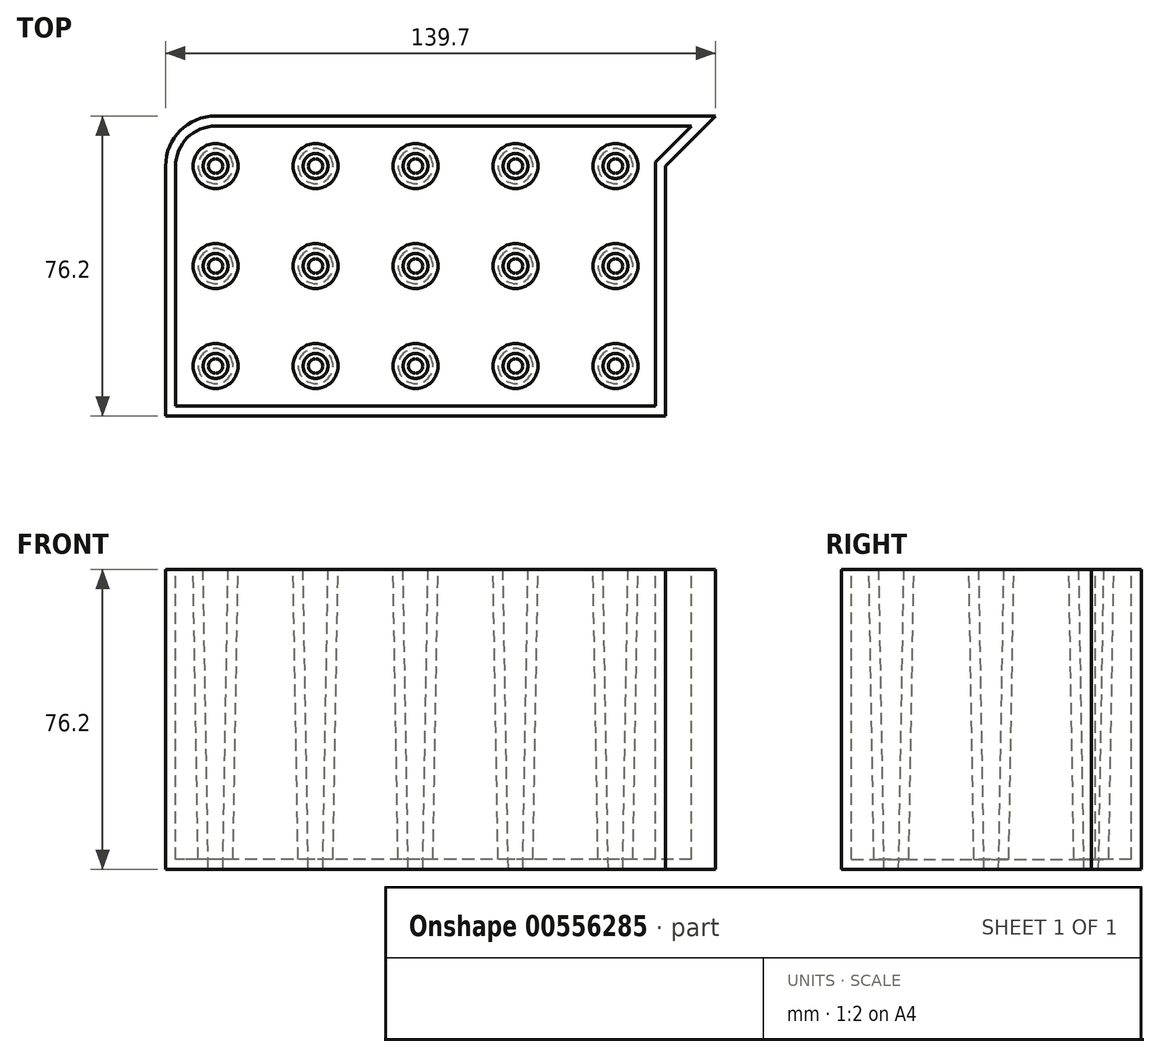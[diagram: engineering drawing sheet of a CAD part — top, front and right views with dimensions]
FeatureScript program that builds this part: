
annotation { "Feature Type Name" : "Feature", "Feature Type Description" : "" }
export const myFeature = defineFeature(function(context is Context, id is Id, definition is map)
    precondition{}
    {
        {
            var Q0;
            Q0=qCreatedBy(makeId("Top.planeOp"),FACE);
            var sketch = newSketch(context, id + "F0", { "sketchPlane" : qUnion([Q0])});
            skLineSegment(sketch, "E0.bottom", {"start": v(63.5, -38.1) * mm, "end": v(-63.5, -38.1) * mm});
            skLineSegment(sketch, "E0.top", {"start": v(76.2, 38.1) * mm, "end": v(-50.8, 38.1) * mm});
            skLineSegment(sketch, "E0.left", {"start": v(63.5, -38.1) * mm, "end": v(63.5, 25.4) * mm});
            skLineSegment(sketch, "E0.right", {"start": v(-63.5, -38.1) * mm, "end": v(-63.5, 25.4) * mm});
            skPoint(sketch, "E0.middle", {"position": v(0, 0) * mm});
            skPoint(sketch, "E1.visualSharp", {"position": v(-63.5, 38.1) * mm});
            skArc(sketch, "E1.filletArc", {"start": v(-50.8, 38.1) * mm, "mid": v(-59.78, 34.38) * mm, "end": v(-63.5, 25.4) * mm});
            skLineSegment(sketch, "E2", {"start": v(76.2, 38.1) * mm, "end": v(63.5, 25.4) * mm});
            skPoint(sketch, "E3.orphan", {"position": v(63.5, 38.1) * mm});
            skSolve(sketch);
        }
        {
            var Q0;
            Q0=makeQuery(id+"F0.imprint","IMPRINT",FACE,{"disambiguationData":[TD([[makeQuery(id+"F0.imprint","IMPRINT",EDGE,{"derivedFrom":sQuery(id+"F0.wireOp",EDGE,"E0.bottom")}),-1.0]])]});
            extrude(context, id + "F1", {"entities" : qUnion([Q0]), "oppositeDirection" : true, "depth" : 76.2 * mm, "offsetDistance" : 25.4 * mm});
        }
        {
            var Q0;
            Q0=makeQuery(id+"F1.opExtrude","CAP_FACE",FACE,{"disambiguationData":[OSD([sQuery(id+"F0.wireOp",EDGE,"E0.bottom"),sQuery(id+"F0.wireOp",EDGE,"E0.top"),sQuery(id+"F0.wireOp",EDGE,"E0.left"),sQuery(id+"F0.wireOp",EDGE,"E0.right"),sQuery(id+"F0.wireOp",EDGE,"E1.filletArc"),sQuery(id+"F0.wireOp",EDGE,"E2")])],"isStart":true});
            var sketch = newSketch(context, id + "F2", { "sketchPlane" : qUnion([Q0])});
            skCircle(sketch, "E4", {"center": v(-50.8, 25.4) * mm, "radius": 3.18 * mm});
            skCircle(sketch, "E5.0.1.0", {"center": v(-50.8, 0) * mm, "radius": 3.18 * mm});
            skCircle(sketch, "E5.0.2.0", {"center": v(-50.8, -25.4) * mm, "radius": 3.18 * mm});
            skCircle(sketch, "E5.1.0.0", {"center": v(-25.4, 25.4) * mm, "radius": 3.18 * mm});
            skCircle(sketch, "E5.1.1.0", {"center": v(-25.4, 0) * mm, "radius": 3.18 * mm});
            skCircle(sketch, "E5.1.2.0", {"center": v(-25.4, -25.4) * mm, "radius": 3.18 * mm});
            skCircle(sketch, "E5.2.0.0", {"center": v(0, 25.4) * mm, "radius": 3.18 * mm});
            skCircle(sketch, "E5.2.1.0", {"center": v(0, 0) * mm, "radius": 3.18 * mm});
            skCircle(sketch, "E5.2.2.0", {"center": v(0, -25.4) * mm, "radius": 3.18 * mm});
            skCircle(sketch, "E5.3.0.0", {"center": v(25.4, 25.4) * mm, "radius": 3.18 * mm});
            skCircle(sketch, "E5.3.1.0", {"center": v(25.4, 0) * mm, "radius": 3.18 * mm});
            skCircle(sketch, "E5.3.2.0", {"center": v(25.4, -25.4) * mm, "radius": 3.18 * mm});
            skCircle(sketch, "E5.4.0.0", {"center": v(50.8, 25.4) * mm, "radius": 3.18 * mm});
            skCircle(sketch, "E5.4.1.0", {"center": v(50.8, 0) * mm, "radius": 3.18 * mm});
            skCircle(sketch, "E5.4.2.0", {"center": v(50.8, -25.4) * mm, "radius": 3.18 * mm});
            skLineSegment(sketch, "E5.direction1", {"start": v(-50.8, 25.4) * mm, "end": v(-25.4, 25.4) * mm, "construction": true});
            skLineSegment(sketch, "E5.direction2", {"start": v(-50.8, 25.4) * mm, "end": v(-50.8, 0) * mm, "construction": true});
            skSolve(sketch);
        }
        {
            var Q0;
            Q0 = qSketchRegion(id + "F2", true);
            extrude(context, id + "F3", {"entities" : qUnion([Q0]), "operationType" : NewBodyOperationType.REMOVE, "endBound" : BoundingType.THROUGH_ALL, "oppositeDirection" : true, "depth" : 47 * mm, "offsetDistance" : 25.4 * mm, "hasDraft" : true, "draftAngle" : 1 * degree, "draftPullDirection" : true});
        }
        {
            var Q0;
            Q0=makeQuery(id+"F1.opExtrude","CAP_FACE",FACE,{"disambiguationData":[OSD([sQuery(id+"F0.wireOp",EDGE,"E0.bottom"),sQuery(id+"F0.wireOp",EDGE,"E0.top"),sQuery(id+"F0.wireOp",EDGE,"E0.left"),sQuery(id+"F0.wireOp",EDGE,"E0.right"),sQuery(id+"F0.wireOp",EDGE,"E1.filletArc"),sQuery(id+"F0.wireOp",EDGE,"E2")])],"isStart":true});
            var Q1;
            Q1=makeQuery(id+"F1.opExtrude","SWEPT_BODY",BODY,{"disambiguationData":[OSD([sQuery(id+"F0.wireOp",EDGE,"E0.bottom"),sQuery(id+"F0.wireOp",EDGE,"E0.top"),sQuery(id+"F0.wireOp",EDGE,"E0.left"),sQuery(id+"F0.wireOp",EDGE,"E0.right"),sQuery(id+"F0.wireOp",EDGE,"E1.filletArc"),sQuery(id+"F0.wireOp",EDGE,"E2")])]});
            shell(context, id + "F4", {"entities" : qUnion([Q0]), "parts" : qUnion([Q1]), "thickness" : 2.54 * mm});
        }
    });
